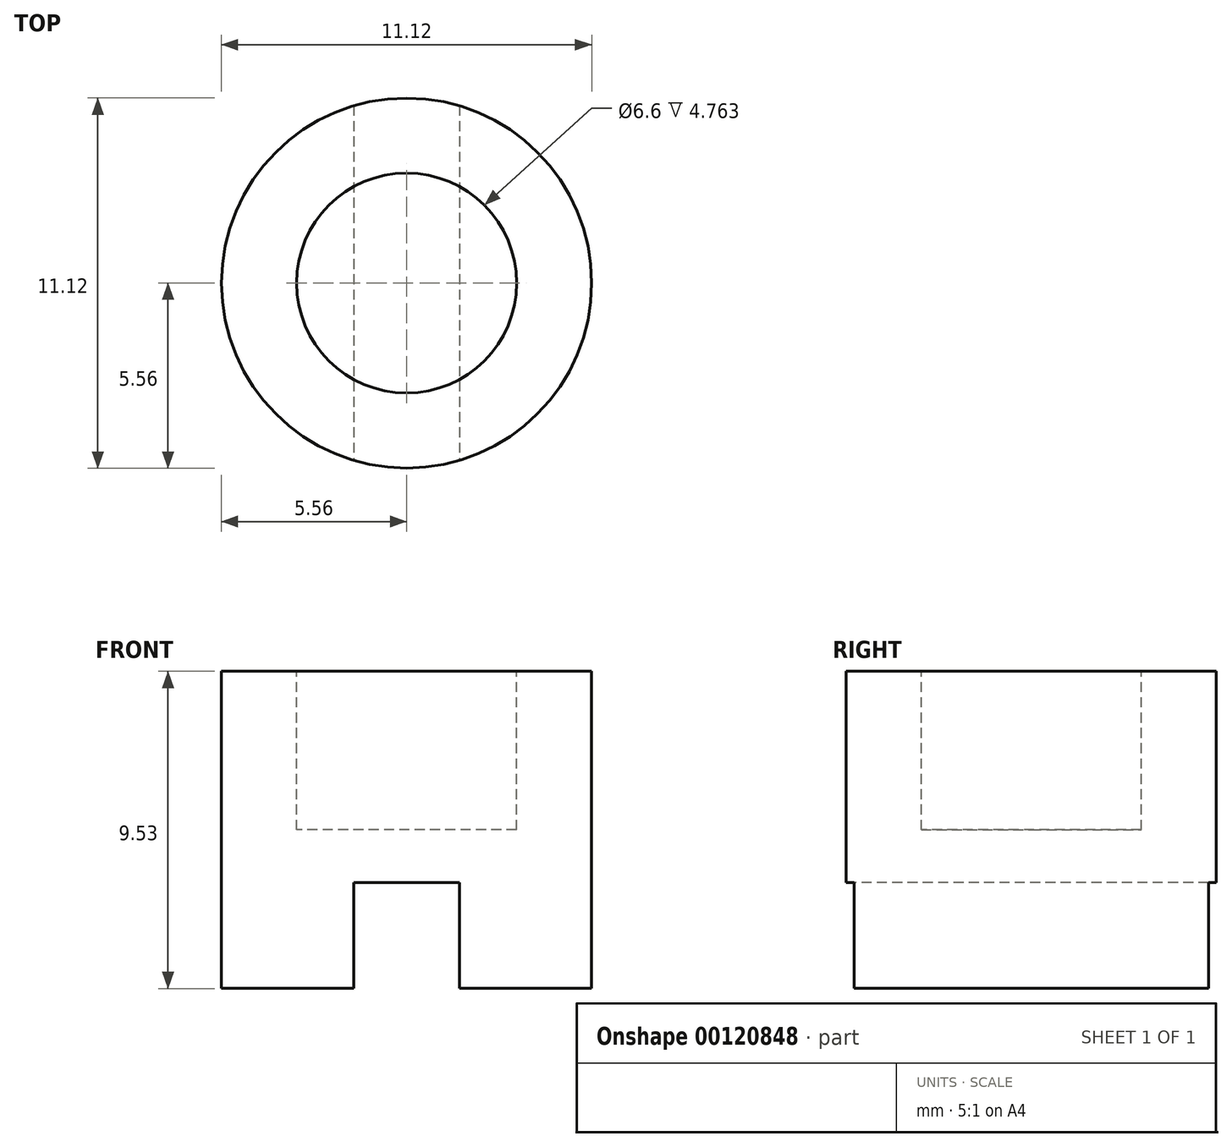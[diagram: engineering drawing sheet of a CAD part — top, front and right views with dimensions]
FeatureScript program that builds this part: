
annotation { "Feature Type Name" : "Feature", "Feature Type Description" : "" }
export const myFeature = defineFeature(function(context is Context, id is Id, definition is map)
    precondition{}
    {
        {
            var Q0;
            Q0=qCreatedBy(makeId("Top.planeOp"),FACE);
            var sketch = newSketch(context, id + "F0", { "sketchPlane" : qUnion([Q0])});
            skCircle(sketch, "E0", {"center": v(0, 0) * mm, "radius": 5.56 * mm});
            skSolve(sketch);
        }
        {
            var Q0;
            Q0 = qSketchRegion(id + "F0", true);
            extrude(context, id + "F1", {"entities" : qUnion([Q0]), "oppositeDirection" : true, "depth" : 9.52 * mm});
        }
        {
            var Q0;
            Q0=makeQuery(id+"F1.opExtrude","CAP_FACE",FACE,{"disambiguationData":[OSD([sQuery(id+"F0.wireOp",EDGE,"E0")])],"isStart":false});
            var sketch = newSketch(context, id + "F2", { "sketchPlane" : qUnion([Q0])});
            skLineSegment(sketch, "E1.bottom", {"start": v(1.59, -5.56) * mm, "end": v(-1.59, -5.56) * mm});
            skLineSegment(sketch, "E1.top", {"start": v(1.59, 5.56) * mm, "end": v(-1.59, 5.56) * mm});
            skLineSegment(sketch, "E1.left", {"start": v(1.59, -5.56) * mm, "end": v(1.59, 5.56) * mm});
            skLineSegment(sketch, "E1.right", {"start": v(-1.59, -5.56) * mm, "end": v(-1.59, 5.56) * mm});
            skSolve(sketch);
        }
        {
            var Q0;
            Q0 = qSketchRegion(id + "F2", true);
            extrude(context, id + "F3", {"entities" : qUnion([Q0]), "operationType" : NewBodyOperationType.REMOVE, "oppositeDirection" : true, "depth" : 3.17 * mm});
        }
        {
            var Q0;
            Q0=makeQuery(id+"F1.opExtrude","CAP_FACE",FACE,{"disambiguationData":[OSD([sQuery(id+"F0.wireOp",EDGE,"E0")])],"isStart":true});
            var sketch = newSketch(context, id + "F4", { "sketchPlane" : qUnion([Q0])});
            skCircle(sketch, "E2", {"center": v(0, 0) * mm, "radius": 3.3 * mm});
            skSolve(sketch);
        }
        {
            var Q0;
            Q0 = qSketchRegion(id + "F4", true);
            extrude(context, id + "F5", {"entities" : qUnion([Q0]), "operationType" : NewBodyOperationType.REMOVE, "oppositeDirection" : true, "depth" : 4.76 * mm});
        }
    });
